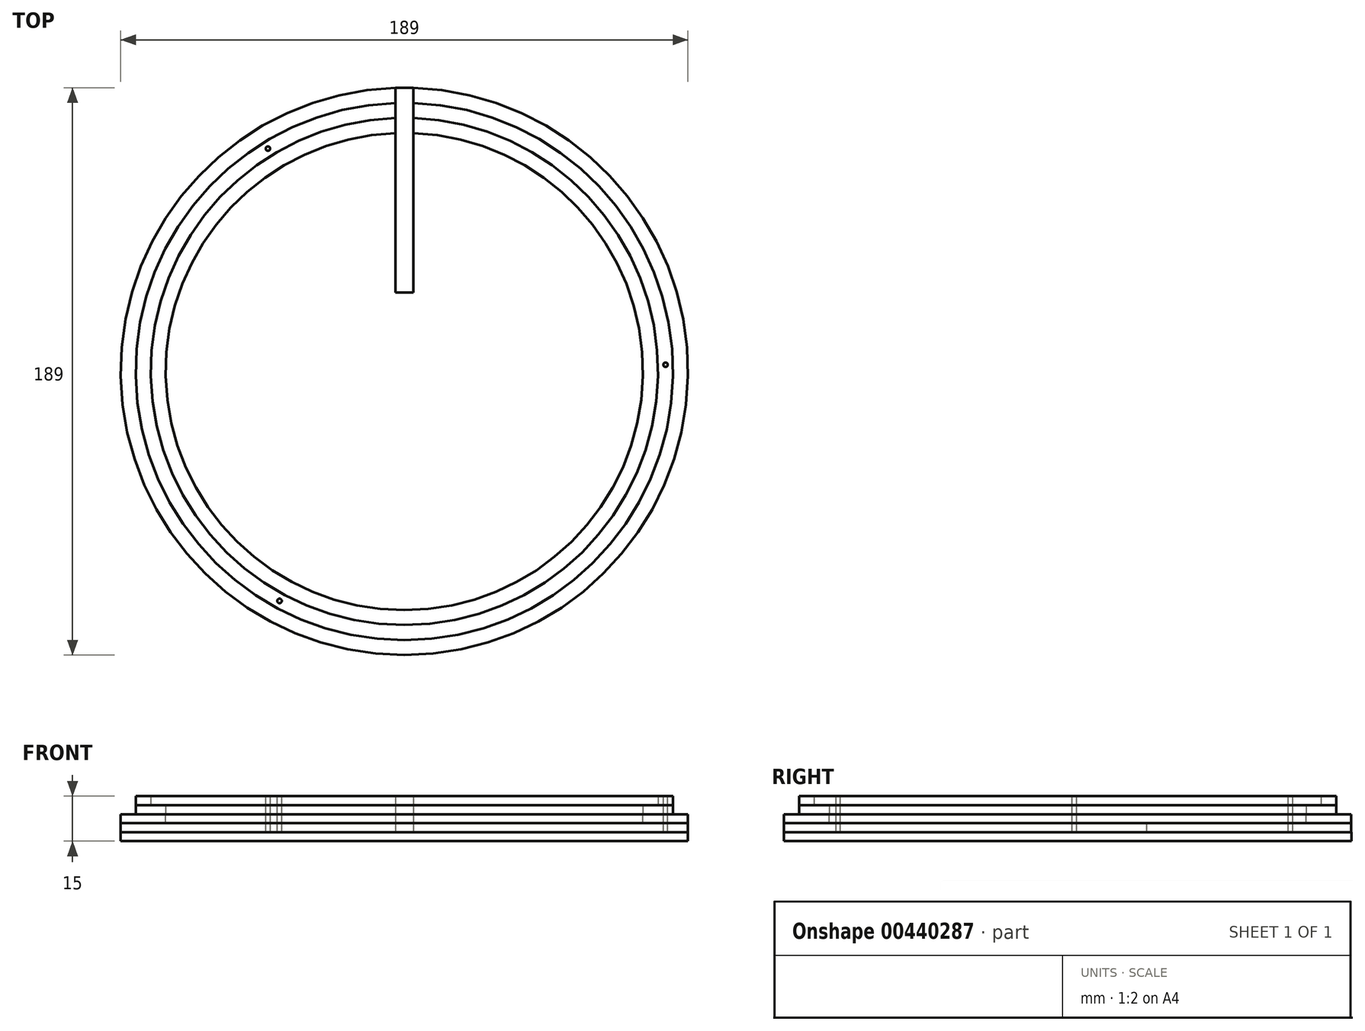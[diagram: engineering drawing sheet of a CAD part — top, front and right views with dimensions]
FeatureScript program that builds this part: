
annotation { "Feature Type Name" : "Feature", "Feature Type Description" : "" }
export const myFeature = defineFeature(function(context is Context, id is Id, definition is map)
    precondition{}
    {
        {
            assignVariable(context, id + "F0", {"name" : "Width1", "anyValue" : 3 * mm});
        }
        {
            var Q0;
            Q0=qCreatedBy(makeId("Top.planeOp"),FACE);
            var sketch = newSketch(context, id + "F1", { "sketchPlane" : qUnion([Q0])});
            skCircle(sketch, "E0", {"center": v(0, 0) * mm, "radius": 89.5 * mm});
            skCircle(sketch, "E1", {"center": v(0, 0) * mm, "radius": 79.5 * mm});
            skSolve(sketch);
        }
        {
            var Q0;
            Q0=makeQuery(id+"F1.imprint","IMPRINT",FACE,{"disambiguationData":[TD([[makeQuery(id+"F1.imprint","IMPRINT",EDGE,{"derivedFrom":sQuery(id+"F1.wireOp",EDGE,"E0")}),1.0]])]});
            extrude(context, id + "F2", {"entities" : qUnion([Q0]), "depth" : getVariable(context, 'Width1')});
        }
        {
            var Q0;
            Q0=makeQuery(id+"F2.opExtrude","CAP_FACE",FACE,{"disambiguationData":[OSD([sQuery(id+"F1.wireOp",EDGE,"E0"),sQuery(id+"F1.wireOp",EDGE,"E1")])],"isStart":false});
            var sketch = newSketch(context, id + "F3", { "sketchPlane" : qUnion([Q0])});
            skCircle(sketch, "E2", {"center": v(0, 0) * mm, "radius": 89.5 * mm});
            skCircle(sketch, "E3", {"center": v(0, 0) * mm, "radius": 84.5 * mm});
            skSolve(sketch);
        }
        {
            var Q0;
            Q0 = qSketchRegion(id + "F3", true);
            extrude(context, id + "F4", {"entities" : qUnion([Q0]), "depth" : getVariable(context, 'Width1')});
        }
        {
            var Q0;
            Q0=makeQuery(id+"F2.opExtrude","CAP_FACE",FACE,{"disambiguationData":[OSD([sQuery(id+"F1.wireOp",EDGE,"E0"),sQuery(id+"F1.wireOp",EDGE,"E1")])],"isStart":true});
            var sketch = newSketch(context, id + "F5", { "sketchPlane" : qUnion([Q0])});
            skCircle(sketch, "E4", {"center": v(0, 0) * mm, "radius": 94.5 * mm});
            skCircle(sketch, "E5", {"center": v(0, 0) * mm, "radius": 79.5 * mm});
            skSolve(sketch);
        }
        {
            var Q0;
            Q0 = qSketchRegion(id + "F5", true);
            extrude(context, id + "F6", {"entities" : qUnion([Q0]), "depth" : getVariable(context, 'Width1')});
        }
        {
            var Q0;
            Q0=makeQuery(id+"F6.opExtrude","CAP_FACE",FACE,{"disambiguationData":[OSD([sQuery(id+"F5.wireOp",EDGE,"E4"),sQuery(id+"F5.wireOp",EDGE,"E5")])],"isStart":false});
            var sketch = newSketch(context, id + "F7", { "sketchPlane" : qUnion([Q0])});
            skCircle(sketch, "E6", {"center": v(0, 0) * mm, "radius": 94.5 * mm});
            skPoint(sketch, "E6.first.point", {"position": v(-7.59, 94.2) * mm});
            skPoint(sketch, "E6.second.point", {"position": v(-80.27, -49.86) * mm});
            skPoint(sketch, "E6.third.point", {"position": v(87.83, -34.87) * mm});
            skSolve(sketch);
        }
        {
            var Q0;
            Q0 = qSketchRegion(id + "F7", true);
            extrude(context, id + "F8", {"entities" : qUnion([Q0]), "depth" : getVariable(context, 'Width1')});
        }
        {
            var Q0;
            Q0=makeQuery(id+"F4.opExtrude","CAP_FACE",FACE,{"disambiguationData":[OSD([sQuery(id+"F3.wireOp",EDGE,"E2"),sQuery(id+"F3.wireOp",EDGE,"E3")])],"isStart":false});
            var sketch = newSketch(context, id + "F9", { "sketchPlane" : qUnion([Q0])});
            skCircle(sketch, "E7", {"center": v(87, 2.22) * mm, "radius": 0.75 * mm});
            skCircle(sketch, "E8.1.0", {"center": v(-45.43, 74.24) * mm, "radius": 0.75 * mm});
            skPoint(sketch, "E8.center", {"position": v(0, 0) * mm});
            skCircle(sketch, "E9.1.2.0", {"center": v(-41.58, -76.46) * mm, "radius": 0.75 * mm});
            skSolve(sketch);
        }
        {
            var Q0;
            Q0 = qSketchRegion(id + "F9", true);
            extrude(context, id + "F10", {"entities" : qUnion([Q0]), "operationType" : NewBodyOperationType.REMOVE, "endBound" : BoundingType.THROUGH_ALL, "oppositeDirection" : true, "depth" : 25 * mm});
        }
        {
            var Q0;
            Q0=makeQuery(id+"F8.opExtrude","CAP_FACE",FACE,{"disambiguationData":[OSD([sQuery(id+"F7.wireOp",EDGE,"E6")])],"isStart":false});
            var sketch = newSketch(context, id + "F11", { "sketchPlane" : qUnion([Q0])});
            skLineSegment(sketch, "E10.bottom", {"start": v(-3, -26.28) * mm, "end": v(3, -26.28) * mm});
            skLineSegment(sketch, "E10.top", {"start": v(-3, -162.72) * mm, "end": v(3, -162.72) * mm});
            skLineSegment(sketch, "E10.left", {"start": v(-3, -26.28) * mm, "end": v(-3, -162.72) * mm});
            skLineSegment(sketch, "E10.right", {"start": v(3, -26.28) * mm, "end": v(3, -162.72) * mm});
            skPoint(sketch, "E10.middle", {"position": v(0, -94.5) * mm});
            skSolve(sketch);
        }
        {
            var Q0;
            {var subQ0=sQuery(id+"F11.wireOp",EDGE,"E10.bottom");Q0=makeQuery(id+"F11.imprint","IMPRINT",FACE,{"disambiguationData":[TD([[makeQuery(id+"F11.imprint","IMPRINT",EDGE,{"derivedFrom":subQ0}),-1.0]])]});}
            extrude(context, id + "F12", {"entities" : qUnion([Q0]), "operationType" : NewBodyOperationType.REMOVE, "oppositeDirection" : true, "depth" : 25 * mm});
        }
        {
            var Q0;
            {var subQ3=sQuery(id+"F11.wireOp",EDGE,"E10.bottom");Q0=makeQuery(id+"F11.imprint","IMPRINT",FACE,{"disambiguationData":[TD([[makeQuery(id+"F11.imprint","IMPRINT",EDGE,{"derivedFrom":subQ3}),1.0]])]});}
            var sketch = newSketch(context, id + "F13", { "sketchPlane" : qUnion([Q0])});
            skCircle(sketch, "E11", {"center": v(0, 0) * mm, "radius": 94.5 * mm});
            skSolve(sketch);
        }
        {
            var Q0;
            Q0 = qSketchRegion(id + "F13", true);
            extrude(context, id + "F14", {"entities" : qUnion([Q0]), "depth" : getVariable(context, 'Width1')});
        }
    });
